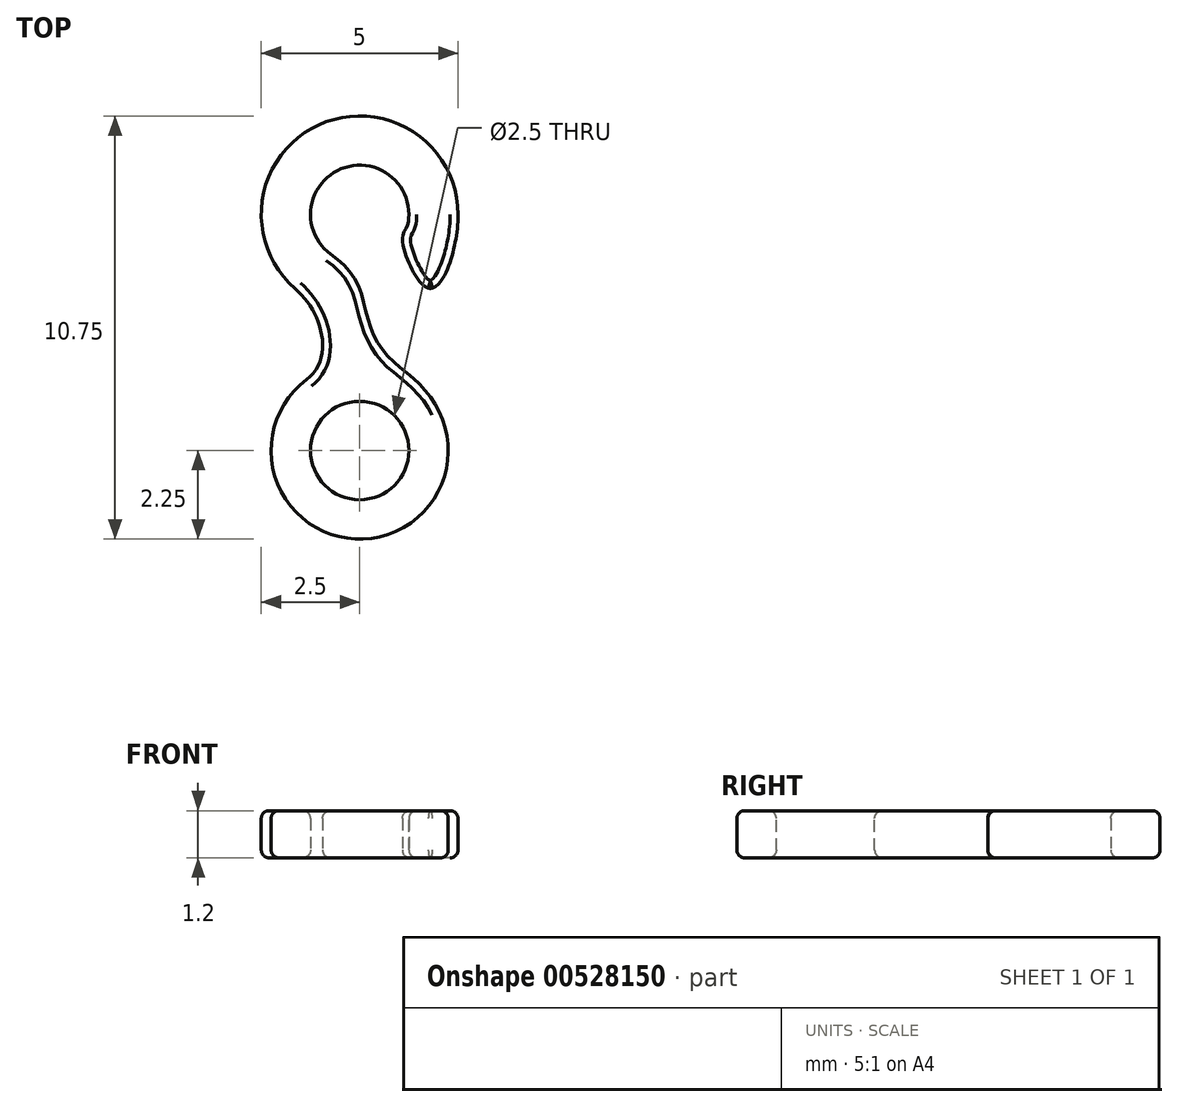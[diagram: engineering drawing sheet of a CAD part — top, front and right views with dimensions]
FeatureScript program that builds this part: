
annotation { "Feature Type Name" : "Feature", "Feature Type Description" : "" }
export const myFeature = defineFeature(function(context is Context, id is Id, definition is map)
    precondition{}
    {
        {
            var Q0;
            Q0=qCreatedBy(makeId("Top.planeOp"),FACE);
            var sketch = newSketch(context, id + "F0", { "sketchPlane" : qUnion([Q0])});
            skArc(sketch, "E0", {"start": v(-1.35, 1.8) * mm, "mid": v(-0.53, -2.19) * mm, "end": v(2.02, 0.99) * mm});
            skLineSegment(sketch, "E1", {"start": v(0, 29.03) * mm, "end": v(0, -4.6) * mm, "construction": true});
            skArc(sketch, "E2", {"start": v(2.5, 6) * mm, "mid": v(-1.04, 8.27) * mm, "end": v(-1.64, 4.11) * mm});
            skArc(sketch, "E3", {"start": v(1.25, 6) * mm, "mid": v(-0.57, 7.11) * mm, "end": v(-0.73, 4.99) * mm});
            skFitSpline(sketch, "E4", {"points": [v(-1.64, 4.11) * mm, v(-0.96, 2.9) * mm, v(-1.35, 1.8) * mm], "startDerivative": vector(2.25, -1.95) * mm, "endDerivative": vector(-2.3, -1.72) * mm});
            skFitSpline(sketch, "E5", {"points": [v(2.02, 0.99) * mm, v(0.7, 2.4) * mm, v(0.17, 3.5) * mm, v(-0.73, 4.99) * mm], "startDerivative": vector(-3.09, 6.31) * mm, "endDerivative": vector(-6.38, 4.62) * mm});
            skFitSpline(sketch, "E6", {"points": [v(1.25, 6) * mm, v(1.09, 5.38) * mm, v(1.77, 4.12) * mm, v(2.5, 6) * mm], "startDerivative": vector(0, -5.29) * mm, "endDerivative": vector(0, 5.7) * mm});
            skSolve(sketch);
        }
        {
            var Q0;
            Q0=makeQuery(id+"F0.imprint","IMPRINT",FACE,{"disambiguationData":[TD([[makeQuery(id+"F0.imprint","IMPRINT",EDGE,{"derivedFrom":sQuery(id+"F0.wireOp",EDGE,"E0")}),1.0]])]});
            extrude(context, id + "F1", {"entities" : qUnion([Q0]), "depth" : 1.2 * mm, "offsetDistance" : 25 * mm});
        }
        {
            var Q0;
            Q0=makeQuery(id+"F1.opExtrude","CAP_FACE",FACE,{"disambiguationData":[OSD([sQuery(id+"F0.wireOp",EDGE,"E0"),sQuery(id+"F0.wireOp",EDGE,"E2"),sQuery(id+"F0.wireOp",EDGE,"E3"),sQuery(id+"F0.wireOp",EDGE,"E4"),sQuery(id+"F0.wireOp",EDGE,"E5"),sQuery(id+"F0.wireOp",EDGE,"E6")])],"isStart":false});
            var sketch = newSketch(context, id + "F2", { "sketchPlane" : qUnion([Q0])});
            skPoint(sketch, "E7", {"position": v(0, 0) * mm});
            skSolve(sketch);
        }
        {
            var Q0;
            Q0=sQuery(id+"F2.wireOp",VERTEX,"E7");
            var Q1;
            Q1=makeQuery(id+"F1.opExtrude","SWEPT_BODY",BODY,{"disambiguationData":[OSD([sQuery(id+"F0.wireOp",EDGE,"E0"),sQuery(id+"F0.wireOp",EDGE,"E2"),sQuery(id+"F0.wireOp",EDGE,"E3"),sQuery(id+"F0.wireOp",EDGE,"E4"),sQuery(id+"F0.wireOp",EDGE,"E5"),sQuery(id+"F0.wireOp",EDGE,"E6")])]});
            hole(context, id + "F3", {"style" : HoleStyle.SIMPLE, "endStyle" : HoleEndStyle.THROUGH, "holeDiameter" : 2.5 * mm, "isTappedThrough" : true, "tappedDepth" : 12 * mm, "tapClearance" : 3, "locations" : qUnion([Q0]), "scope" : qUnion([Q1])});
        }
        {
            var Q0;
            Q0=makeQuery(id+"F1.opExtrude","CAP_FACE",FACE,{"disambiguationData":[OSD([sQuery(id+"F0.wireOp",EDGE,"E0"),sQuery(id+"F0.wireOp",EDGE,"E2"),sQuery(id+"F0.wireOp",EDGE,"E3"),sQuery(id+"F0.wireOp",EDGE,"E4"),sQuery(id+"F0.wireOp",EDGE,"E5"),sQuery(id+"F0.wireOp",EDGE,"E6")])],"isStart":false});
            var Q1;
            Q1=makeQuery(id+"F1.opExtrude","CAP_FACE",FACE,{"disambiguationData":[OSD([sQuery(id+"F0.wireOp",EDGE,"E0"),sQuery(id+"F0.wireOp",EDGE,"E2"),sQuery(id+"F0.wireOp",EDGE,"E3"),sQuery(id+"F0.wireOp",EDGE,"E4"),sQuery(id+"F0.wireOp",EDGE,"E5"),sQuery(id+"F0.wireOp",EDGE,"E6")])],"isStart":true});
            fillet(context, id + "F4", {"entities" : qUnion([Q0, Q1]), "radius" : .2 * mm, "tangentPropagation" : true, "allowEdgeOverflow" : false});
        }
    });
